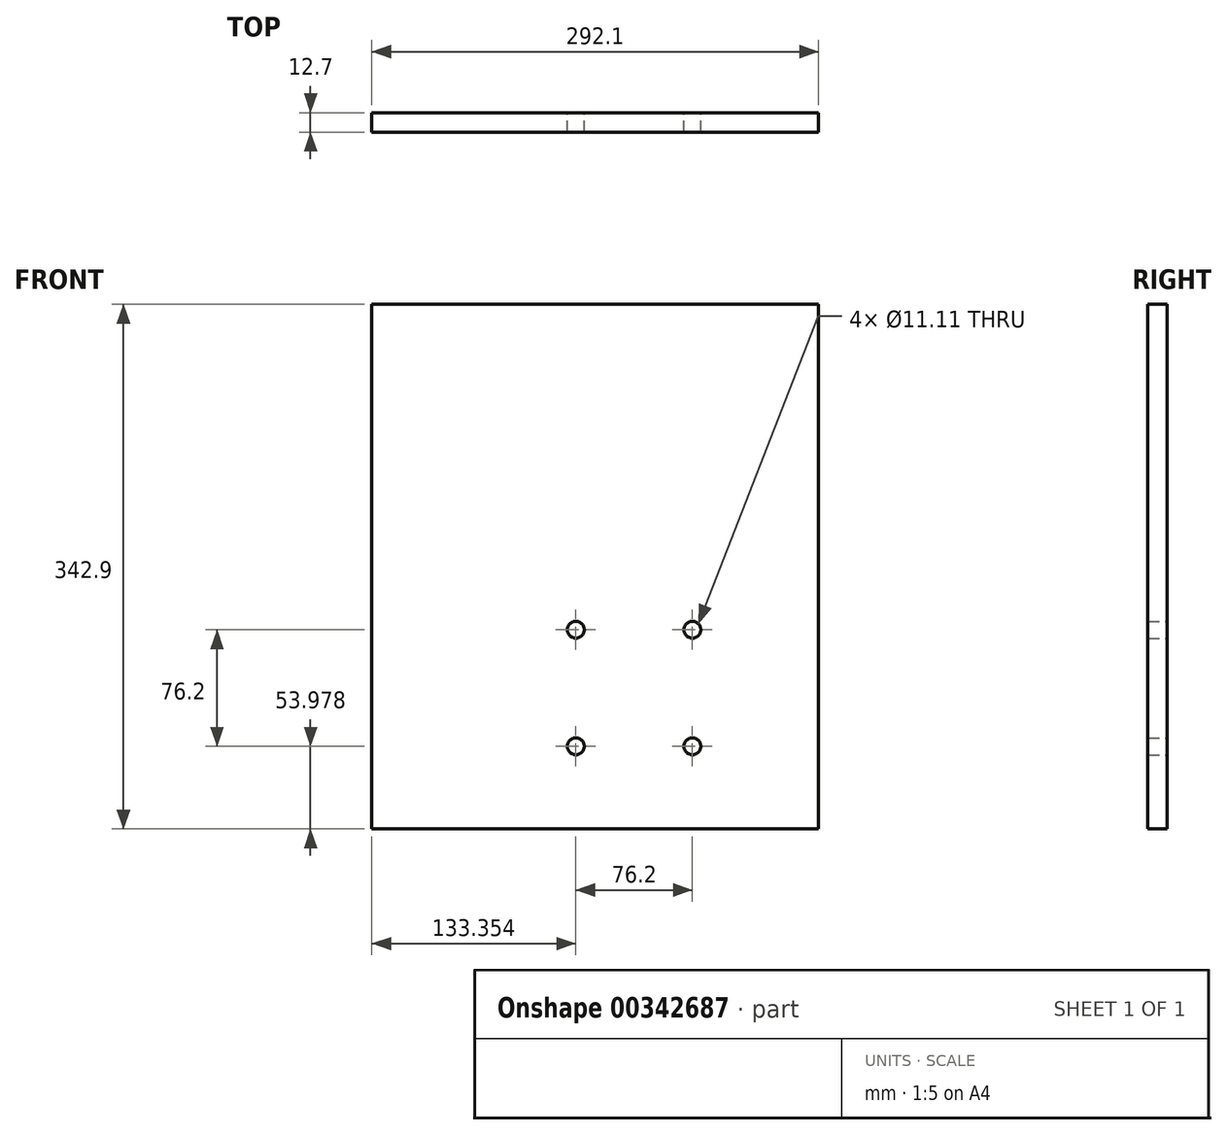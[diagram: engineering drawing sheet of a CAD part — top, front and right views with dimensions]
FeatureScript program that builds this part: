
annotation { "Feature Type Name" : "Feature", "Feature Type Description" : "" }
export const myFeature = defineFeature(function(context is Context, id is Id, definition is map)
    precondition{}
    {
        {
            var Q0;
            Q0=qCreatedBy(makeId("Front.planeOp"),FACE);
            var sketch = newSketch(context, id + "F0", { "sketchPlane" : qUnion([Q0])});
            skLineSegment(sketch, "E0.bottom", {"start": v(-289.07, 445.74) * mm, "end": v(3.03, 445.74) * mm});
            skLineSegment(sketch, "E0.top", {"start": v(-289.07, 102.84) * mm, "end": v(3.03, 102.84) * mm});
            skLineSegment(sketch, "E0.left", {"start": v(-289.07, 445.74) * mm, "end": v(-289.07, 102.84) * mm});
            skLineSegment(sketch, "E0.right", {"start": v(3.03, 445.74) * mm, "end": v(3.03, 102.84) * mm});
            skCircle(sketch, "E1", {"center": v(-155.72, 156.82) * mm, "radius": 5.56 * mm});
            skCircle(sketch, "E2.0.1.0", {"center": v(-155.72, 233.02) * mm, "radius": 5.56 * mm});
            skCircle(sketch, "E2.1.0.0", {"center": v(-79.52, 156.82) * mm, "radius": 5.56 * mm});
            skCircle(sketch, "E2.1.1.0", {"center": v(-79.52, 233.02) * mm, "radius": 5.56 * mm});
            skLineSegment(sketch, "E2.direction1", {"start": v(-155.72, 156.82) * mm, "end": v(-79.52, 156.82) * mm, "construction": true});
            skLineSegment(sketch, "E2.direction2", {"start": v(-155.72, 156.82) * mm, "end": v(-155.72, 233.02) * mm, "construction": true});
            skSolve(sketch);
        }
        {
            var Q0;
            Q0=makeQuery(id+"F0.imprint","IMPRINT",FACE,{"disambiguationData":[TD([[makeQuery(id+"F0.imprint","IMPRINT",EDGE,{"derivedFrom":sQuery(id+"F0.wireOp",EDGE,"E0.bottom")}),-1.0]])]});
            extrude(context, id + "F1", {"entities" : qUnion([Q0]), "depth" : 12.7 * mm});
        }
    });
